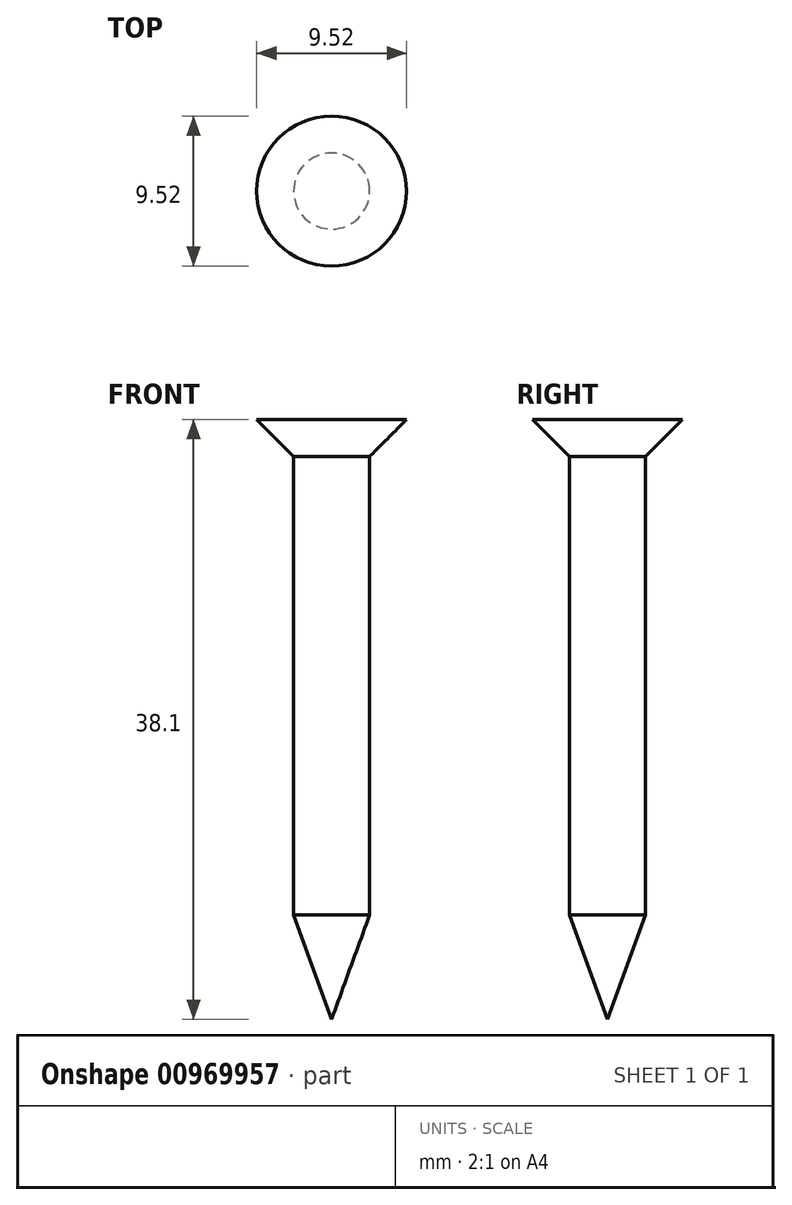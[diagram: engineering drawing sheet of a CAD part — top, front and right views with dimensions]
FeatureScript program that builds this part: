
annotation { "Feature Type Name" : "Feature", "Feature Type Description" : "" }
export const myFeature = defineFeature(function(context is Context, id is Id, definition is map)
    precondition{}
    {
        {
            var Q0;
            Q0=qCreatedBy(makeId("Front.planeOp"),FACE);
            var sketch = newSketch(context, id + "F0", { "sketchPlane" : qUnion([Q0])});
            skLineSegment(sketch, "E0", {"start": v(0, 56.88) * mm, "end": v(0, -89.13) * mm});
            skSolve(sketch);
        }
        {
            var Q0;
            Q0=qCreatedBy(makeId("Front.planeOp"),FACE);
            var sketch = newSketch(context, id + "F1", { "sketchPlane" : qUnion([Q0])});
            skLineSegment(sketch, "E1", {"start": v(0, 0) * mm, "end": v(4.76, 0) * mm});
            skLineSegment(sketch, "E2", {"start": v(4.76, 0) * mm, "end": v(2.41, -2.35) * mm});
            skLineSegment(sketch, "E3", {"start": v(2.41, -2.35) * mm, "end": v(2.41, -31.47) * mm});
            skLineSegment(sketch, "E4", {"start": v(2.41, -31.47) * mm, "end": v(0, -38.1) * mm});
            skLineSegment(sketch, "E5", {"start": v(0, -38.1) * mm, "end": v(0, 0) * mm});
            skSolve(sketch);
        }
        {
            var Q0;
            Q0 = qSketchRegion(id + "F1", true);
            var Q1;
            Q1=sQuery(id+"F0.wireOp",EDGE,"E0");
            revolve(context, id + "F2", {"surfaceOperationType" : NewSurfaceOperationType.NEW, "entities" : qUnion([Q0]), "axis" : qUnion([Q1]), "revolveType" : RevolveType.FULL});
        }
    });
